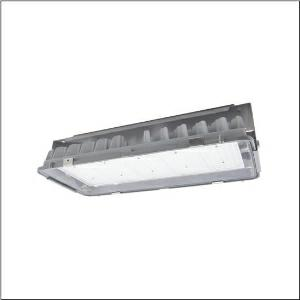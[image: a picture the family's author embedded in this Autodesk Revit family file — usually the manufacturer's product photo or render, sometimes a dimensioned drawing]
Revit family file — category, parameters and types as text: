
# Revit family: highbay_11xtreme_51hf62da4mma
name_source: partatom
category: Lighting Fixtures
units: mm (PartAtom-declared; Revit-internal decimal feet)

## family parameters
Cut with Voids When Loaded = No
Host = Face
Light Source = No
Part Type = Normal
Room Calculation Point = No
Round Connector Dimension = Use Diameter
Shared = No

## types (1)
- --- (1 x LED, 31100 lm, 170.9 W, 4000K)
    Apparent Load = 171 VA
    CIE Flux Codes = 84 96 100 100 100
    Color Rendering = 80
    Color Temperature = 4000K
    Default Elevation = 1800 mm
    Description = Highbay 11Xtreme, high bay luminaire, primary light control with lens, of PMMA, primary optical cover: cover, of toughened safety glass, light emission: direct distribution, primary light characteristic: symmetric, installation type: suspended mounting, surface-mounted, 1x LED module,for 1x LED, rated luminous flux: 31.100lm, luminous efficacy: 182lm/W, light colour: 840, colour temperature: 4000K, control gear: DALI 2, with cable H07RN-F 5x 1.5mm², mains connection: 220..240V, AC, 50/60Hz, cable length: 1,5m, rated input power: 171W, luminaire housing, of diecast aluminium, coated, silver, length: 595mm, width: 280mm, height: 195mm, protection rating (complete): IP66, insulation class (complete): insulation class I (protective earthing), certification: CE, ENEC, UKCA, protection symbol: D, ball protection: ball impact resistant according to DIN VDE 0710 part 13 (with chain suspension), impact resistance: IK08, permissible operating ambient temperature: -25..+60°C, reducing of maximum allowable ambient temperature of 5°C with ceiling mounting, packaging unit: 1 piece
    Height = 157 mm
    Lamp = 1 x LED
    Lamp Light Flux = 31100 lm
    Lamp Power = 170.9 W
    Lamp count = 1
    Length = 593 mm
    Luminous efficacy = 182 lm/W
    Manufacturer = Siteco
    ModVariant = No
    Model = 51HF62DA4MMA
    Mounting Place = Ceiling
    Mounting Type = Pendant
    Number of Poles = 1
    OnlyDefault = Yes
    Power Factor = 1
    Product Name = Highbay 11Xtreme
    Product group = high bay luminaire
    ProductGroupID = 901
    Protection Class = Protection class I
    Protection Degree = IP 66
    RLX_Detail_Level = 1
    RLX_Emergency_Light_Flux = 0 lm
    RLX_Emergency_Type = 0
    RLX_Emergency_Type_DB = No
    RlxData = <blob elided: 28341 chars, md5=6c7beb84>
    Socket = socket
    Standby Power = 0 W
    System Light Flux = 31100 lm
    System Power = 171 W
    Type Comments = factory setting: luminous flux: 100 % | dim-lin: 254 | 1133 mA
    Type Image = l_1258342.jpg
    URL = http://relux.com
    VarID = @adj_083236
    Voltage = 0 V
    Weight = 0.00 kg
    Width = 568 mm

## geometry (parser evidence)
native form markers: Blend x4, Sweep x11
no freeform markers — native parametric forms only
